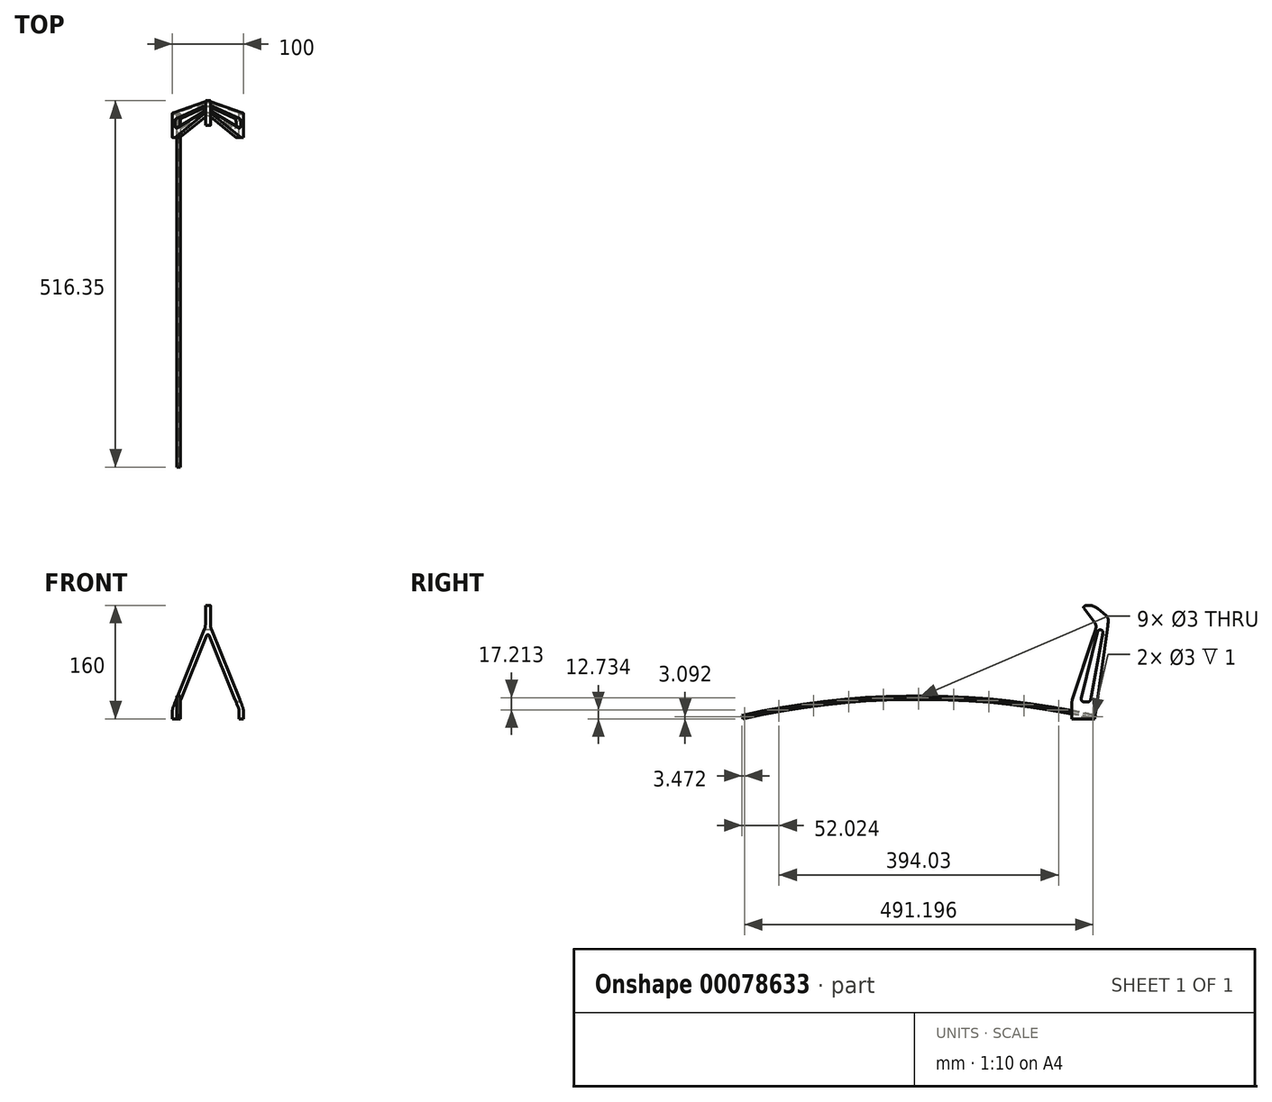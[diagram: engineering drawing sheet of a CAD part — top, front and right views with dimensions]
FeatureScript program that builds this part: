
annotation { "Feature Type Name" : "Feature", "Feature Type Description" : "" }
export const myFeature = defineFeature(function(context is Context, id is Id, definition is map)
    precondition{}
    {
        {
            var Q0;
            Q0=qCreatedBy(makeId("Front.planeOp"),FACE);
            var sketch = newSketch(context, id + "F0", { "sketchPlane" : qUnion([Q0])});
            skLineSegment(sketch, "E0", {"start": v(-44, 0) * mm, "end": v(-50, 0) * mm});
            skLineSegment(sketch, "E1", {"start": v(44, 0) * mm, "end": v(50, 0) * mm});
            skLineSegment(sketch, "E2", {"start": v(-50, 0) * mm, "end": v(-50, 10.5) * mm});
            skLineSegment(sketch, "E3", {"start": v(-48.54, 18) * mm, "end": v(-4.96, 125.87) * mm});
            skLineSegment(sketch, "E4", {"start": v(-3.5, 133.37) * mm, "end": v(-3.5, 160) * mm});
            skLineSegment(sketch, "E5", {"start": v(-3.5, 160) * mm, "end": v(3.5, 160) * mm});
            skLineSegment(sketch, "E6", {"start": v(3.5, 160) * mm, "end": v(3.5, 133.37) * mm});
            skLineSegment(sketch, "E7", {"start": v(4.96, 125.87) * mm, "end": v(48.54, 18) * mm});
            skLineSegment(sketch, "E8", {"start": v(50, 10.5) * mm, "end": v(50, 0) * mm});
            skLineSegment(sketch, "E9", {"start": v(0, 0) * mm, "end": v(0, 160) * mm, "construction": true});
            skPoint(sketch, "E10.visualSharp", {"position": v(-3.5, 129.48) * mm});
            skArc(sketch, "E10.filletArc", {"start": v(-4.96, 125.87) * mm, "mid": v(-3.87, 129.55) * mm, "end": v(-3.5, 133.37) * mm});
            skPoint(sketch, "E11.visualSharp", {"position": v(3.5, 129.48) * mm});
            skArc(sketch, "E11.filletArc", {"start": v(3.5, 133.37) * mm, "mid": v(3.87, 129.55) * mm, "end": v(4.96, 125.87) * mm});
            skPoint(sketch, "E12.visualSharp", {"position": v(-50, 14.39) * mm});
            skArc(sketch, "E12.filletArc", {"start": v(-48.54, 18) * mm, "mid": v(-49.63, 14.32) * mm, "end": v(-50, 10.5) * mm});
            skPoint(sketch, "E13.visualSharp", {"position": v(50, 14.39) * mm});
            skArc(sketch, "E13.filletArc", {"start": v(50, 10.5) * mm, "mid": v(49.63, 14.32) * mm, "end": v(48.54, 18) * mm});
            skLineSegment(sketch, "E14.0", {"start": v(-42.98, 15.74) * mm, "end": v(-1.85, 117.54) * mm});
            skLineSegment(sketch, "E15.0", {"start": v(1.85, 117.54) * mm, "end": v(42.98, 15.74) * mm});
            skLineSegment(sketch, "E16.0", {"start": v(44, 10.5) * mm, "end": v(44, 0) * mm});
            skLineSegment(sketch, "E17.0", {"start": v(-44, 0) * mm, "end": v(-44, 10.5) * mm});
            skArc(sketch, "E18.filletArc", {"start": v(1.85, 117.54) * mm, "mid": v(0, 118.79) * mm, "end": v(-1.85, 117.54) * mm});
            skPoint(sketch, "E19.visualSharp", {"position": v(-44, 13.22) * mm});
            skArc(sketch, "E19.filletArc", {"start": v(-42.98, 15.74) * mm, "mid": v(-43.74, 13.17) * mm, "end": v(-44, 10.5) * mm});
            skPoint(sketch, "E20.visualSharp", {"position": v(44, 13.22) * mm});
            skArc(sketch, "E20.filletArc", {"start": v(44, 10.5) * mm, "mid": v(43.74, 13.17) * mm, "end": v(42.98, 15.74) * mm});
            skSolve(sketch);
        }
        {
            var Q0;
            Q0=makeQuery(id+"F0.imprint","IMPRINT",FACE,{"disambiguationData":[TD([[makeQuery(id+"F0.imprint","IMPRINT",EDGE,{"derivedFrom":sQuery(id+"F0.wireOp",EDGE,"E0")}),-1.0]])]});
            extrude(context, id + "F1", {"entities" : qUnion([Q0]), "endBound" : BoundingType.SYMMETRIC, "depth" : 150 * mm});
        }
        {
            var Q0;
            Q0=qCreatedBy(makeId("Right.planeOp"),FACE);
            var sketch = newSketch(context, id + "F2", { "sketchPlane" : qUnion([Q0])});
            skLineSegment(sketch, "E21", {"start": v(0, 0) * mm, "end": v(19.2, 136.62) * mm});
            skLineSegment(sketch, "E22", {"start": v(15.73, 145.67) * mm, "end": v(4.23, 155.32) * mm});
            skArc(sketch, "E23", {"start": v(-8.38, 120) * mm, "mid": v(-7.78, 120.02) * mm, "end": v(-7.17, 120.05) * mm});
            skLineSegment(sketch, "E24", {"start": v(0, 0) * mm, "end": v(-32.5, 0) * mm});
            skLineSegment(sketch, "E25", {"start": v(-32.5, 0) * mm, "end": v(-32.5, 21) * mm});
            skPoint(sketch, "E26.visualSharp", {"position": v(19.97, 142.1) * mm});
            skArc(sketch, "E26.filletArc", {"start": v(19.2, 136.62) * mm, "mid": v(18.63, 141.6) * mm, "end": v(15.73, 145.67) * mm});
            skArc(sketch, "E27", {"start": v(-8.38, 120) * mm, "mid": v(-7.77, 120) * mm, "end": v(-7.17, 120.05) * mm});
            skLineSegment(sketch, "E28", {"start": v(1.3, 126.87) * mm, "end": v(-31.5, 27.25) * mm});
            skPoint(sketch, "E29.visualSharp", {"position": v(-32.5, 24.2) * mm});
            skArc(sketch, "E29.filletArc", {"start": v(-31.5, 27.25) * mm, "mid": v(-32.25, 24.17) * mm, "end": v(-32.5, 21) * mm});
            skLineSegment(sketch, "E30", {"start": v(-0.2, 135.99) * mm, "end": v(-15.22, 156.1) * mm});
            skArc(sketch, "E31.trimOffspring", {"start": v(1.3, 126.87) * mm, "mid": v(1.67, 131.61) * mm, "end": v(-0.2, 135.99) * mm});
            skArc(sketch, "E32.trimOffspring", {"start": v(4.23, 155.32) * mm, "mid": v(-4.49, 159.57) * mm, "end": v(-14.18, 159.22) * mm});
            skArc(sketch, "E33", {"start": v(-14.18, 159.22) * mm, "mid": v(-15.52, 157.93) * mm, "end": v(-15.22, 156.1) * mm});
            skArc(sketch, "E34", {"start": v(11.53, 120.77) * mm, "mid": v(8.44, 125.41) * mm, "end": v(3.71, 122.45) * mm});
            skLineSegment(sketch, "E35", {"start": v(11.53, 120.77) * mm, "end": v(-5.8, 27.27) * mm});
            skLineSegment(sketch, "E36", {"start": v(-15.23, 24) * mm, "end": v(-9.73, 24) * mm});
            skLineSegment(sketch, "E37", {"start": v(11.15, 152.9) * mm, "end": v(-19.11, 28.95) * mm});
            skPoint(sketch, "E38.visualSharp", {"position": v(-20.32, 24) * mm});
            skArc(sketch, "E38.filletArc", {"start": v(-19.11, 28.95) * mm, "mid": v(-18.38, 25.53) * mm, "end": v(-15.23, 24) * mm});
            skPoint(sketch, "E39.visualSharp", {"position": v(-6.4, 24) * mm});
            skArc(sketch, "E39.filletArc", {"start": v(-9.73, 24) * mm, "mid": v(-7.17, 24.92) * mm, "end": v(-5.8, 27.27) * mm});
            skSolve(sketch);
        }
        {
            var Q0;
            Q0=makeQuery(id+"F2.imprint","IMPRINT",FACE,{"disambiguationData":[TD([[makeQuery(id+"F2.imprint","IMPRINT",EDGE,{"derivedFrom":sQuery(id+"F2.wireOp",EDGE,"E21")}),1.0]])]});
            extrude(context, id + "F3", {"entities" : qUnion([Q0]), "endBound" : BoundingType.SYMMETRIC, "depth" : 155 * mm});
        }
        {
            var Q0;
            Q0=makeQuery(id+"F3.opExtrude","SWEPT_BODY",BODY,{"disambiguationData":[OSD([sQuery(id+"F2.wireOp",EDGE,"E21"),sQuery(id+"F2.wireOp",EDGE,"E22"),sQuery(id+"F2.wireOp",EDGE,"E24"),sQuery(id+"F2.wireOp",EDGE,"E25"),sQuery(id+"F2.wireOp",EDGE,"E26.filletArc"),sQuery(id+"F2.wireOp",EDGE,"E28"),sQuery(id+"F2.wireOp",EDGE,"E29.filletArc"),sQuery(id+"F2.wireOp",EDGE,"E30"),sQuery(id+"F2.wireOp",EDGE,"E31.trimOffspring"),sQuery(id+"F2.wireOp",EDGE,"E32.trimOffspring"),sQuery(id+"F2.wireOp",EDGE,"E33"),sQuery(id+"F2.wireOp",EDGE,"E34"),sQuery(id+"F2.wireOp",EDGE,"E35"),sQuery(id+"F2.wireOp",EDGE,"E36"),sQuery(id+"F2.wireOp",EDGE,"E37"),sQuery(id+"F2.wireOp",EDGE,"E38.filletArc"),sQuery(id+"F2.wireOp",EDGE,"E39.filletArc")])]});
            var Q1;
            Q1=makeQuery(id+"F1.opExtrude","SWEPT_BODY",BODY,{"disambiguationData":[OSD([sQuery(id+"F0.wireOp",EDGE,"E0"),sQuery(id+"F0.wireOp",EDGE,"E1"),sQuery(id+"F0.wireOp",EDGE,"E2"),sQuery(id+"F0.wireOp",EDGE,"E3"),sQuery(id+"F0.wireOp",EDGE,"E4"),sQuery(id+"F0.wireOp",EDGE,"E5"),sQuery(id+"F0.wireOp",EDGE,"E6"),sQuery(id+"F0.wireOp",EDGE,"E7"),sQuery(id+"F0.wireOp",EDGE,"E8"),sQuery(id+"F0.wireOp",EDGE,"E10.filletArc"),sQuery(id+"F0.wireOp",EDGE,"E11.filletArc"),sQuery(id+"F0.wireOp",EDGE,"E12.filletArc"),sQuery(id+"F0.wireOp",EDGE,"E13.filletArc"),sQuery(id+"F0.wireOp",EDGE,"E14.0"),sQuery(id+"F0.wireOp",EDGE,"E15.0"),sQuery(id+"F0.wireOp",EDGE,"E16.0"),sQuery(id+"F0.wireOp",EDGE,"E17.0"),sQuery(id+"F0.wireOp",EDGE,"E18.filletArc"),sQuery(id+"F0.wireOp",EDGE,"E19.filletArc"),sQuery(id+"F0.wireOp",EDGE,"E20.filletArc")])]});
            booleanBodies(context, id + "F4", {"operationType" : BooleanOperationType.INTERSECTION, "tools" : qUnion([Q0, Q1])});
        }
        {
            var Q0;
            Q0=makeQuery(id+"F1.opExtrude","SWEPT_FACE",FACE,{"disambiguationData":[OSD([sQuery(id+"F0.wireOp",EDGE,"E17.0")])]});
            var sketch = newSketch(context, id + "F5", { "sketchPlane" : qUnion([Q0])});
            skLineSegment(sketch, "E40", {"start": v(0, 0) * mm, "end": v(-495.96, 0) * mm, "construction": true});
            skArc(sketch, "E41", {"start": v(0, 0) * mm, "mid": v(-247.98, 27.45) * mm, "end": v(-495.96, 0) * mm});
            skSolve(sketch);
        }
        {
            var Q0;
            Q0=sQuery(id+"F5.wireOp",VERTEX,"E40.start");
            var Q1;
            Q1=sQuery(id+"F5.wireOp",EDGE,"E41");
            cPlane(context, id + "F6", {"entities" : qUnion([Q0, Q1]), "cplaneType" : CPlaneType.CURVE_POINT, "offset" : 150 * mm, "width" : 150 * mm, "height" : 150 * mm});
        }
        {
            var Q0;
            Q0=qCreatedBy(id+"F6.planeOp",FACE);
            var sketch = newSketch(context, id + "F7", { "sketchPlane" : qUnion([Q0])});
            skLineSegment(sketch, "E42", {"start": v(-44, 0) * mm, "end": v(-39, 0) * mm});
            skLineSegment(sketch, "E43", {"start": v(-39, 0) * mm, "end": v(-39, 1) * mm});
            skLineSegment(sketch, "E44", {"start": v(-39, 5) * mm, "end": v(-44, 5) * mm});
            skLineSegment(sketch, "E45", {"start": v(-44, 5) * mm, "end": v(-44, 4) * mm});
            skLineSegment(sketch, "E46", {"start": v(-44, 4) * mm, "end": v(-42, 4) * mm});
            skLineSegment(sketch, "E47", {"start": v(-42, 4) * mm, "end": v(-42, 1) * mm});
            skLineSegment(sketch, "E48", {"start": v(-42, 1) * mm, "end": v(-44, 1) * mm});
            skLineSegment(sketch, "E49.trimOffspring", {"start": v(-44, 1) * mm, "end": v(-44, 0) * mm});
            skLineSegment(sketch, "E50", {"start": v(-39, 4) * mm, "end": v(-41, 4) * mm});
            skLineSegment(sketch, "E51", {"start": v(-41, 4) * mm, "end": v(-41, 1) * mm});
            skLineSegment(sketch, "E52", {"start": v(-41, 1) * mm, "end": v(-39, 1) * mm});
            skLineSegment(sketch, "E53.trimOffspring", {"start": v(-39, 4) * mm, "end": v(-39, 5) * mm});
            skSolve(sketch);
        }
        {
            var Q0;
            Q0=makeQuery(id+"F7.imprint","IMPRINT",FACE,{"disambiguationData":[TD([[makeQuery(id+"F7.imprint","IMPRINT",EDGE,{"derivedFrom":sQuery(id+"F7.wireOp",EDGE,"E42")}),1.0]])]});
            var Q1;
            Q1=sQuery(id+"F5.wireOp",EDGE,"E41");
            sweep(context, id + "F8", {"operationType" : NewBodyOperationType.ADD, "profiles" : qUnion([Q0]), "path" : qUnion([Q1])});
        }
        {
            var Q0;
            Q0=makeQuery(id+"F8.opSweep","SWEPT_FACE",FACE,{"disambiguationData":[OSD([sQuery(id+"F5.wireOp",EDGE,"E41"),sQuery(id+"F7.wireOp",EDGE,"E51")])]});
            var sketch = newSketch(context, id + "F9", { "sketchPlane" : qUnion([Q0])});
            skArc(sketch, "E54.0", {"start": v(0.22, 0.98) * mm, "mid": v(-247.98, 28.45) * mm, "end": v(-496.18, 0.98) * mm, "construction": true});
            skArc(sketch, "E55.0", {"start": v(0.55, 2.44) * mm, "mid": v(-247.98, 29.95) * mm, "end": v(-496.5, 2.44) * mm, "construction": true});
            skCircle(sketch, "E56", {"center": v(-493.58, 3.1) * mm, "radius": 1.5 * mm});
            skCircle(sketch, "E57", {"center": v(-2.38, 3.1) * mm, "radius": 1.5 * mm});
            skCircle(sketch, "E58", {"center": v(-445.03, 12.73) * mm, "radius": 1.5 * mm});
            skCircle(sketch, "E59", {"center": v(-396.1, 20.25) * mm, "radius": 1.5 * mm});
            skCircle(sketch, "E60", {"center": v(-346.9, 25.63) * mm, "radius": 1.5 * mm});
            skCircle(sketch, "E61", {"center": v(-297.5, 28.87) * mm, "radius": 1.5 * mm});
            skCircle(sketch, "E62", {"center": v(-248.01, 29.95) * mm, "radius": 1.5 * mm});
            skCircle(sketch, "E63", {"center": v(-198.52, 28.87) * mm, "radius": 1.5 * mm});
            skCircle(sketch, "E64", {"center": v(-149.13, 25.64) * mm, "radius": 1.5 * mm});
            skCircle(sketch, "E65", {"center": v(-99.92, 20.26) * mm, "radius": 1.5 * mm});
            skCircle(sketch, "E66", {"center": v(-51, 12.75) * mm, "radius": 1.5 * mm});
            skSolve(sketch);
        }
        {
            var Q0;
            {var subQ0=sQuery(id+"F9.wireOp",EDGE,"E56");var subQ1=sQuery(id+"F7.wireOp",EDGE,"E51");var subQ2=sQuery(id+"F5.wireOp",EDGE,"E41");var subQ3=makeQuery(id+"F9.imprint","INTERSECT",VERTEX,{"derivedFrom":[makeQuery(id+"F8.opSweep","SWEPT_EDGE",EDGE,{"disambiguationData":[OSD([subQ2,sQuery(id+"F7.wireOp",EDGE,"E50"),subQ1])]}),subQ0]});Q0=makeQuery(id+"F9.imprint","IMPRINT",FACE,{"disambiguationData":[TD([[makeQuery(id+"F9.imprint","IMPRINT",EDGE,{"disambiguationData":[TD([[subQ3,-1.0]])],"derivedFrom":subQ0}),1.0]])]});}
            var Q1;
            {var subQ0=sQuery(id+"F9.wireOp",EDGE,"E58");var subQ1=sQuery(id+"F7.wireOp",EDGE,"E51");var subQ2=sQuery(id+"F5.wireOp",EDGE,"E41");var subQ3=makeQuery(id+"F9.imprint","INTERSECT",VERTEX,{"derivedFrom":[makeQuery(id+"F8.opSweep","SWEPT_EDGE",EDGE,{"disambiguationData":[OSD([subQ2,sQuery(id+"F7.wireOp",EDGE,"E50"),subQ1])]}),subQ0]});Q1=makeQuery(id+"F9.imprint","IMPRINT",FACE,{"disambiguationData":[TD([[makeQuery(id+"F9.imprint","IMPRINT",EDGE,{"disambiguationData":[TD([[subQ3,-1.0]])],"derivedFrom":subQ0}),1.0]])]});}
            var Q2;
            {var subQ0=sQuery(id+"F9.wireOp",EDGE,"E59");var subQ1=sQuery(id+"F7.wireOp",EDGE,"E51");var subQ2=sQuery(id+"F5.wireOp",EDGE,"E41");var subQ3=makeQuery(id+"F9.imprint","INTERSECT",VERTEX,{"derivedFrom":[makeQuery(id+"F8.opSweep","SWEPT_EDGE",EDGE,{"disambiguationData":[OSD([subQ2,sQuery(id+"F7.wireOp",EDGE,"E50"),subQ1])]}),subQ0]});Q2=makeQuery(id+"F9.imprint","IMPRINT",FACE,{"disambiguationData":[TD([[makeQuery(id+"F9.imprint","IMPRINT",EDGE,{"disambiguationData":[TD([[subQ3,-1.0]])],"derivedFrom":subQ0}),1.0]])]});}
            var Q3;
            {var subQ0=sQuery(id+"F9.wireOp",EDGE,"E60");var subQ1=sQuery(id+"F7.wireOp",EDGE,"E51");var subQ2=sQuery(id+"F5.wireOp",EDGE,"E41");var subQ3=makeQuery(id+"F9.imprint","INTERSECT",VERTEX,{"derivedFrom":[makeQuery(id+"F8.opSweep","SWEPT_EDGE",EDGE,{"disambiguationData":[OSD([subQ2,sQuery(id+"F7.wireOp",EDGE,"E50"),subQ1])]}),subQ0]});Q3=makeQuery(id+"F9.imprint","IMPRINT",FACE,{"disambiguationData":[TD([[makeQuery(id+"F9.imprint","IMPRINT",EDGE,{"disambiguationData":[TD([[subQ3,-1.0]])],"derivedFrom":subQ0}),1.0]])]});}
            var Q4;
            {var subQ0=sQuery(id+"F9.wireOp",EDGE,"E61");var subQ1=sQuery(id+"F7.wireOp",EDGE,"E51");var subQ2=sQuery(id+"F5.wireOp",EDGE,"E41");var subQ3=makeQuery(id+"F9.imprint","INTERSECT",VERTEX,{"derivedFrom":[makeQuery(id+"F8.opSweep","SWEPT_EDGE",EDGE,{"disambiguationData":[OSD([subQ2,sQuery(id+"F7.wireOp",EDGE,"E50"),subQ1])]}),subQ0]});Q4=makeQuery(id+"F9.imprint","IMPRINT",FACE,{"disambiguationData":[TD([[makeQuery(id+"F9.imprint","IMPRINT",EDGE,{"disambiguationData":[TD([[subQ3,-1.0]])],"derivedFrom":subQ0}),1.0]])]});}
            var Q5;
            {var subQ0=sQuery(id+"F9.wireOp",EDGE,"E62");var subQ1=sQuery(id+"F7.wireOp",EDGE,"E51");var subQ2=sQuery(id+"F5.wireOp",EDGE,"E41");var subQ3=makeQuery(id+"F9.imprint","INTERSECT",VERTEX,{"derivedFrom":[makeQuery(id+"F8.opSweep","SWEPT_EDGE",EDGE,{"disambiguationData":[OSD([subQ2,sQuery(id+"F7.wireOp",EDGE,"E50"),subQ1])]}),subQ0]});Q5=makeQuery(id+"F9.imprint","IMPRINT",FACE,{"disambiguationData":[TD([[makeQuery(id+"F9.imprint","IMPRINT",EDGE,{"disambiguationData":[TD([[subQ3,-1.0]])],"derivedFrom":subQ0}),1.0]])]});}
            var Q6;
            {var subQ0=sQuery(id+"F9.wireOp",EDGE,"E63");var subQ1=sQuery(id+"F7.wireOp",EDGE,"E51");var subQ2=sQuery(id+"F5.wireOp",EDGE,"E41");var subQ3=makeQuery(id+"F9.imprint","INTERSECT",VERTEX,{"derivedFrom":[makeQuery(id+"F8.opSweep","SWEPT_EDGE",EDGE,{"disambiguationData":[OSD([subQ2,sQuery(id+"F7.wireOp",EDGE,"E50"),subQ1])]}),subQ0]});Q6=makeQuery(id+"F9.imprint","IMPRINT",FACE,{"disambiguationData":[TD([[makeQuery(id+"F9.imprint","IMPRINT",EDGE,{"disambiguationData":[TD([[subQ3,-1.0]])],"derivedFrom":subQ0}),1.0]])]});}
            var Q7;
            {var subQ0=sQuery(id+"F9.wireOp",EDGE,"E64");var subQ1=sQuery(id+"F7.wireOp",EDGE,"E51");var subQ2=sQuery(id+"F5.wireOp",EDGE,"E41");var subQ3=makeQuery(id+"F9.imprint","INTERSECT",VERTEX,{"derivedFrom":[makeQuery(id+"F8.opSweep","SWEPT_EDGE",EDGE,{"disambiguationData":[OSD([subQ2,sQuery(id+"F7.wireOp",EDGE,"E50"),subQ1])]}),subQ0]});Q7=makeQuery(id+"F9.imprint","IMPRINT",FACE,{"disambiguationData":[TD([[makeQuery(id+"F9.imprint","IMPRINT",EDGE,{"disambiguationData":[TD([[subQ3,-1.0]])],"derivedFrom":subQ0}),1.0]])]});}
            var Q8;
            {var subQ0=sQuery(id+"F9.wireOp",EDGE,"E65");var subQ1=sQuery(id+"F7.wireOp",EDGE,"E51");var subQ2=sQuery(id+"F5.wireOp",EDGE,"E41");var subQ3=makeQuery(id+"F9.imprint","INTERSECT",VERTEX,{"derivedFrom":[makeQuery(id+"F8.opSweep","SWEPT_EDGE",EDGE,{"disambiguationData":[OSD([subQ2,sQuery(id+"F7.wireOp",EDGE,"E50"),subQ1])]}),subQ0]});Q8=makeQuery(id+"F9.imprint","IMPRINT",FACE,{"disambiguationData":[TD([[makeQuery(id+"F9.imprint","IMPRINT",EDGE,{"disambiguationData":[TD([[subQ3,-1.0]])],"derivedFrom":subQ0}),1.0]])]});}
            var Q9;
            {var subQ0=sQuery(id+"F9.wireOp",EDGE,"E66");var subQ1=sQuery(id+"F7.wireOp",EDGE,"E51");var subQ2=sQuery(id+"F5.wireOp",EDGE,"E41");var subQ3=makeQuery(id+"F9.imprint","INTERSECT",VERTEX,{"derivedFrom":[makeQuery(id+"F8.opSweep","SWEPT_EDGE",EDGE,{"disambiguationData":[OSD([subQ2,sQuery(id+"F7.wireOp",EDGE,"E50"),subQ1])]}),subQ0]});Q9=makeQuery(id+"F9.imprint","IMPRINT",FACE,{"disambiguationData":[TD([[makeQuery(id+"F9.imprint","IMPRINT",EDGE,{"disambiguationData":[TD([[subQ3,-1.0]])],"derivedFrom":subQ0}),1.0]])]});}
            var Q10;
            {var subQ0=sQuery(id+"F9.wireOp",EDGE,"E57");var subQ1=sQuery(id+"F7.wireOp",EDGE,"E51");var subQ2=sQuery(id+"F5.wireOp",EDGE,"E41");var subQ3=makeQuery(id+"F9.imprint","INTERSECT",VERTEX,{"derivedFrom":[makeQuery(id+"F8.opSweep","SWEPT_EDGE",EDGE,{"disambiguationData":[OSD([subQ2,sQuery(id+"F7.wireOp",EDGE,"E50"),subQ1])]}),subQ0]});Q10=makeQuery(id+"F9.imprint","IMPRINT",FACE,{"disambiguationData":[TD([[makeQuery(id+"F9.imprint","IMPRINT",EDGE,{"disambiguationData":[TD([[subQ3,-1.0]])],"derivedFrom":subQ0}),1.0]])]});}
            extrude(context, id + "F10", {"entities" : qUnion([Q0, Q1, Q2, Q3, Q4, Q5, Q6, Q7, Q8, Q9, Q10]), "operationType" : NewBodyOperationType.REMOVE, "oppositeDirection" : true, "depth" : 1 * mm});
        }
    });
